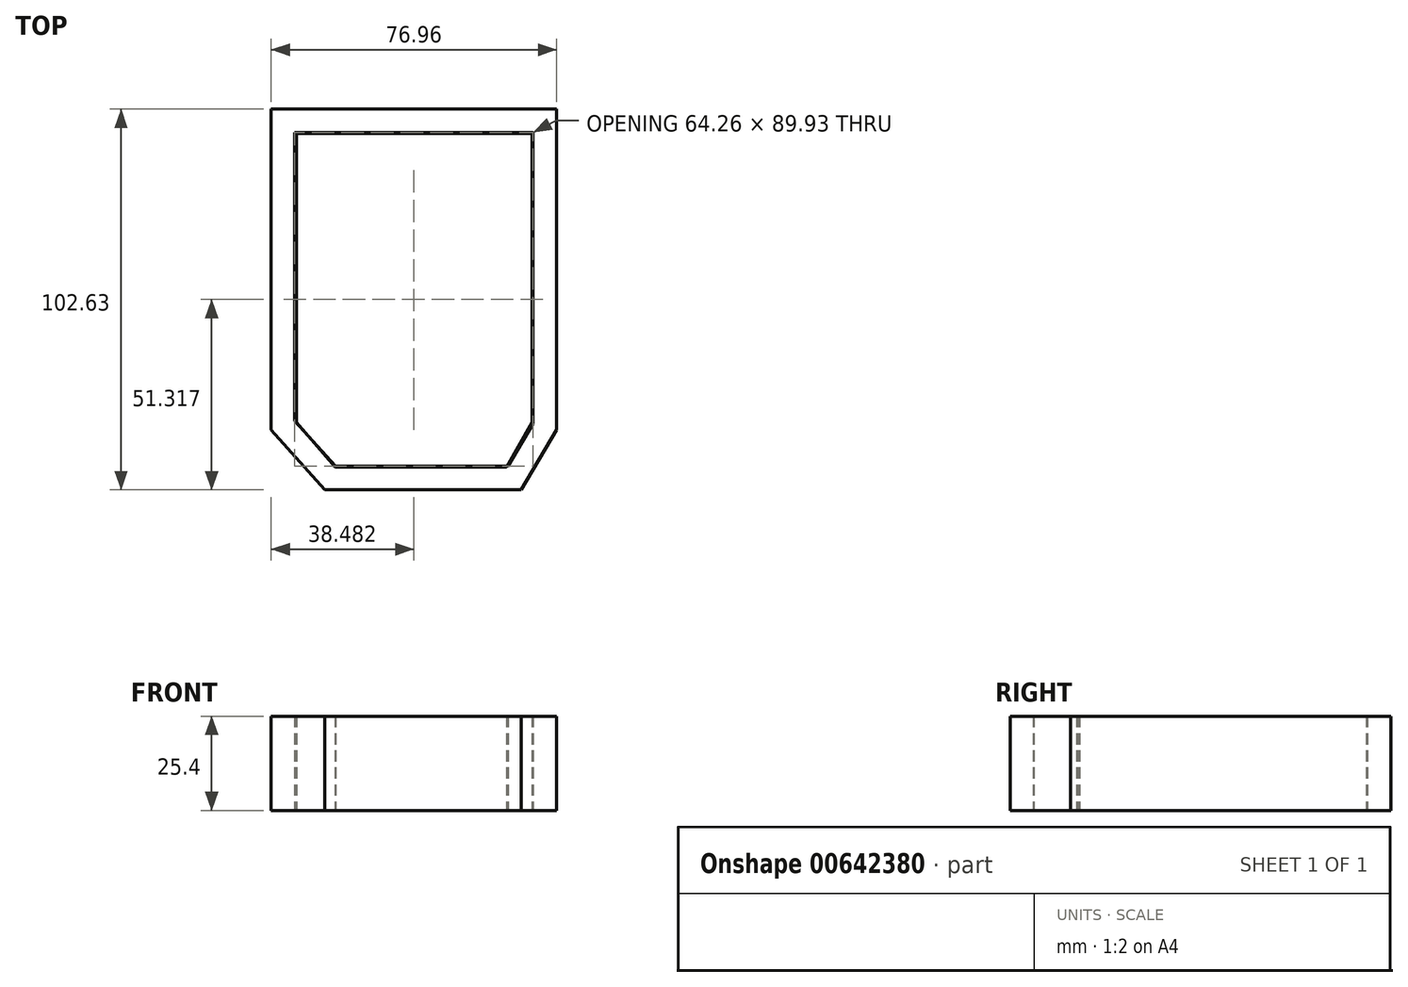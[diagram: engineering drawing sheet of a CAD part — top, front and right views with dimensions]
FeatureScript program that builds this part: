
annotation { "Feature Type Name" : "Feature", "Feature Type Description" : "" }
export const myFeature = defineFeature(function(context is Context, id is Id, definition is map)
    precondition{}
    {
        {
            var Q0;
            Q0=qCreatedBy(makeId("Top.planeOp"),FACE);
            var sketch = newSketch(context, id + "F0", { "sketchPlane" : qUnion([Q0])});
            skLineSegment(sketch, "E0.bottom", {"start": v(0, 0) * mm, "end": v(76.96, 0) * mm});
            skLineSegment(sketch, "E0.top", {"start": v(0, 0) * mm, "end": v(76.96, 0) * mm});
            skLineSegment(sketch, "E0.left", {"start": v(0, 0) * mm, "end": v(0, 0) * mm});
            skLineSegment(sketch, "E0.right", {"start": v(76.96, 0) * mm, "end": v(76.96, 0) * mm});
            skLineSegment(sketch, "E1", {"start": v(76.96, 0) * mm, "end": v(76.96, -86.47) * mm});
            skLineSegment(sketch, "E2", {"start": v(76.96, -86.47) * mm, "end": v(67.44, -102.63) * mm});
            skLineSegment(sketch, "E3", {"start": v(67.44, -102.63) * mm, "end": v(14.5, -102.63) * mm});
            skLineSegment(sketch, "E4", {"start": v(14.5, -102.63) * mm, "end": v(0, -86.47) * mm});
            skLineSegment(sketch, "E5", {"start": v(0, -86.47) * mm, "end": v(0, 0) * mm});
            skLineSegment(sketch, "E6.0", {"start": v(6.35, -84.03) * mm, "end": v(6.35, -6.35) * mm});
            skLineSegment(sketch, "E6.1", {"start": v(70.61, -6.35) * mm, "end": v(70.61, -84.73) * mm});
            skLineSegment(sketch, "E6.2", {"start": v(70.61, -84.73) * mm, "end": v(63.81, -96.28) * mm});
            skLineSegment(sketch, "E6.3", {"start": v(6.35, -6.35) * mm, "end": v(70.61, -6.35) * mm});
            skLineSegment(sketch, "E6.4", {"start": v(63.81, -96.28) * mm, "end": v(17.34, -96.28) * mm});
            skLineSegment(sketch, "E6.5", {"start": v(17.34, -96.28) * mm, "end": v(6.35, -84.03) * mm});
            skSolve(sketch);
        }
        {
            var Q0;
            Q0 = qSketchRegion(id + "F0", true);
            extrude(context, id + "F1", {"entities" : qUnion([Q0]), "depth" : 25.4 * mm, "offsetDistance" : 25.4 * mm});
        }
        {
            var Q0;
            Q0=qCreatedBy(makeId("Top.planeOp"),FACE);
            var sketch = newSketch(context, id + "F2", { "sketchPlane" : qUnion([Q0])});
            skLineSegment(sketch, "E7.bottom", {"start": v(6.84, -6.61) * mm, "end": v(70.35, -6.61) * mm});
            skLineSegment(sketch, "E7.top", {"start": v(6.84, -6.89) * mm, "end": v(70.35, -6.89) * mm});
            skLineSegment(sketch, "E7.left", {"start": v(6.84, -6.61) * mm, "end": v(6.84, -6.89) * mm});
            skLineSegment(sketch, "E7.right", {"start": v(70.35, -6.61) * mm, "end": v(70.35, -6.89) * mm});
            skLineSegment(sketch, "E8.bottom", {"start": v(70.35, -6.61) * mm, "end": v(70.35, -6.61) * mm});
            skLineSegment(sketch, "E8.top", {"start": v(70.35, -84.42) * mm, "end": v(70.35, -84.42) * mm});
            skLineSegment(sketch, "E8.left", {"start": v(70.35, -6.61) * mm, "end": v(70.35, -84.42) * mm});
            skLineSegment(sketch, "E8.right", {"start": v(70.35, -6.61) * mm, "end": v(70.35, -84.42) * mm});
            skLineSegment(sketch, "E9.bottom", {"start": v(6.84, -6.61) * mm, "end": v(6.84, -6.61) * mm});
            skLineSegment(sketch, "E9.top", {"start": v(6.84, -84.42) * mm, "end": v(6.84, -84.42) * mm});
            skLineSegment(sketch, "E9.left", {"start": v(6.84, -6.61) * mm, "end": v(6.84, -84.42) * mm});
            skLineSegment(sketch, "E9.right", {"start": v(6.84, -6.61) * mm, "end": v(6.84, -84.42) * mm});
            skLineSegment(sketch, "E10", {"start": v(6.84, -84.42) * mm, "end": v(17.29, -96.51) * mm});
            skLineSegment(sketch, "E11.bottom", {"start": v(17.29, -96.51) * mm, "end": v(63.47, -96.51) * mm});
            skLineSegment(sketch, "E11.top", {"start": v(17.29, -96.51) * mm, "end": v(63.47, -96.51) * mm});
            skLineSegment(sketch, "E11.left", {"start": v(17.29, -96.51) * mm, "end": v(17.29, -96.51) * mm});
            skLineSegment(sketch, "E11.right", {"start": v(63.47, -96.51) * mm, "end": v(63.47, -96.51) * mm});
            skLineSegment(sketch, "E12", {"start": v(63.47, -96.51) * mm, "end": v(70.35, -84.42) * mm});
            skSolve(sketch);
        }
        {
            var Q0;
            Q0 = qSketchRegion(id + "F2", true);
            extrude(context, id + "F3", {"entities" : qUnion([Q0]), "depth" : 25.4 * mm, "offsetDistance" : 25.4 * mm});
        }
    });
